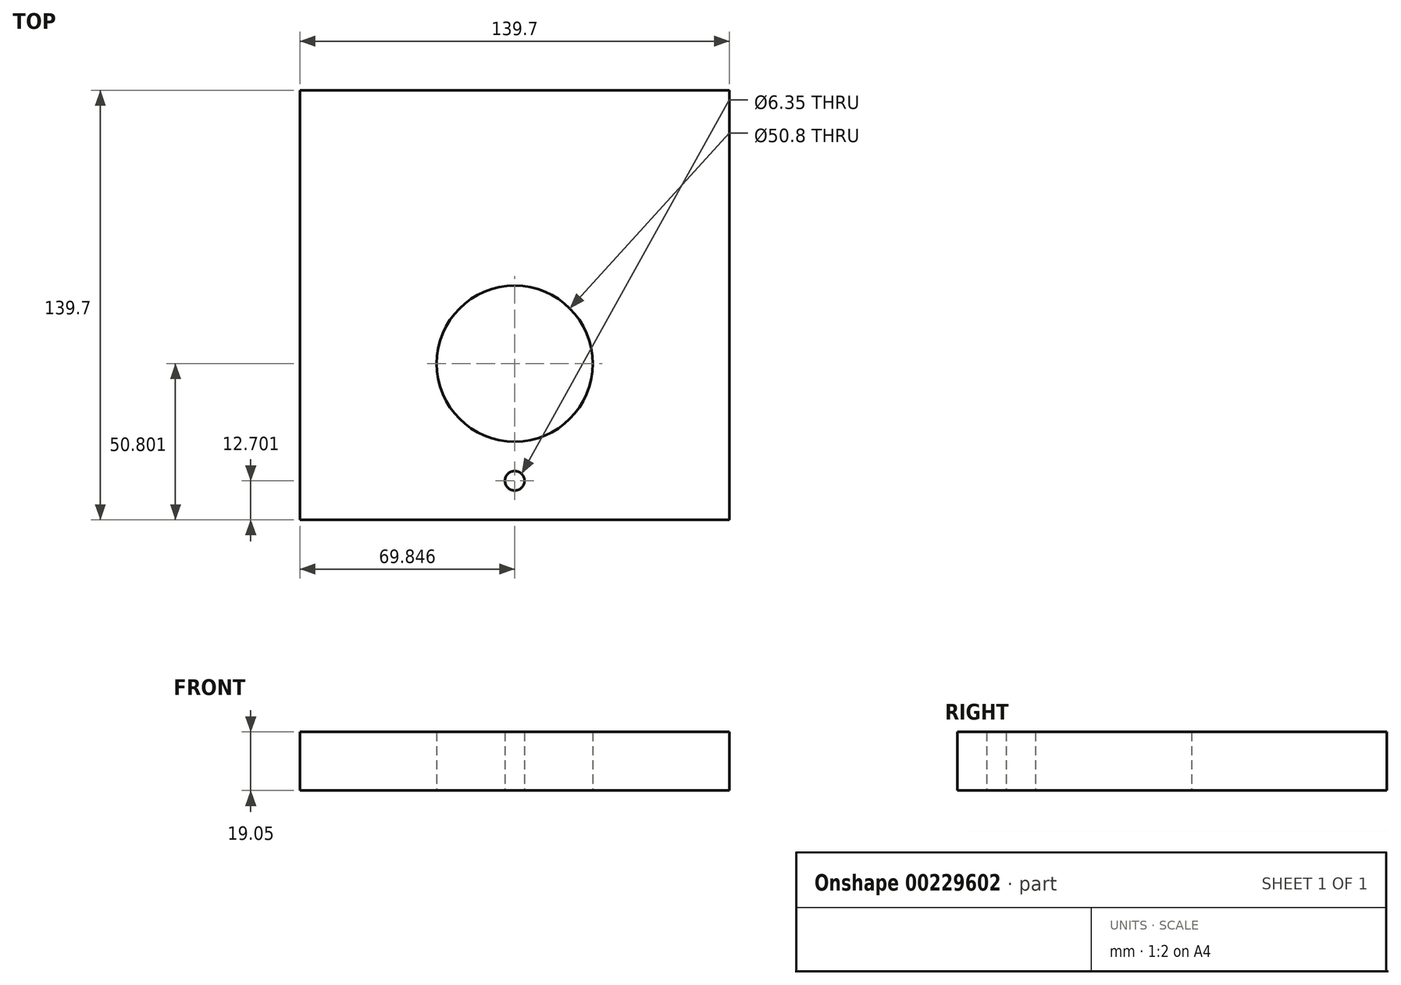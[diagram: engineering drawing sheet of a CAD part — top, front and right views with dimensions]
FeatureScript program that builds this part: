
annotation { "Feature Type Name" : "Feature", "Feature Type Description" : "" }
export const myFeature = defineFeature(function(context is Context, id is Id, definition is map)
    precondition{}
    {
        {
            var Q0;
            Q0=qCreatedBy(makeId("Top.planeOp"),FACE);
            var sketch = newSketch(context, id + "F0", { "sketchPlane" : qUnion([Q0])});
            skLineSegment(sketch, "E0.bottom", {"start": v(69.87, -70.97) * mm, "end": v(-69.83, -70.97) * mm});
            skLineSegment(sketch, "E0.top", {"start": v(69.87, 68.73) * mm, "end": v(-69.83, 68.73) * mm});
            skLineSegment(sketch, "E0.left", {"start": v(69.87, -70.97) * mm, "end": v(69.87, 68.73) * mm});
            skLineSegment(sketch, "E0.right", {"start": v(-69.83, -70.97) * mm, "end": v(-69.83, 68.73) * mm});
            skPoint(sketch, "E0.middle", {"position": v(0.02, -1.12) * mm});
            skLineSegment(sketch, "E1", {"start": v(0.02, -70.97) * mm, "end": v(0.02, -58.27) * mm});
            skLineSegment(sketch, "E2", {"start": v(0.02, -58.27) * mm, "end": v(0.02, -20.17) * mm});
            skCircle(sketch, "E3", {"center": v(0.02, -20.17) * mm, "radius": 25.4 * mm});
            skCircle(sketch, "E4", {"center": v(0.02, -58.27) * mm, "radius": 3.18 * mm});
            skSolve(sketch);
        }
        {
            var Q0;
            Q0 = qSketchRegion(id + "F0", true);
            extrude(context, id + "F1", {"entities" : qUnion([Q0]), "depth" : 19.05 * mm});
        }
    });
